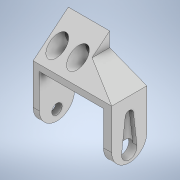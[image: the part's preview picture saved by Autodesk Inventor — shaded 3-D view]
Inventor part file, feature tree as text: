
AUTODESK INVENTOR PART (.ipt)
format: ipt  version: 2022.1 (Build 261234000, 234)  size: 200,192 bytes
history: native  units: mm
features: extrude x8, sketch x7, fillet x1
ambient origin geometry x8: Origin, YZ Plane, XZ Plane, XY Plane, X Axis, Y Axis, Z Axis, Center Point
bodies: Solid1 (feature_tree)
feature tree (16):
  extrude  "Extrusion1"  Depth=3.0mm
  extrude  "Extrusion2"  Depth=4.0mm
  extrude  "Extrusion4"  Depth=38.0mm
  extrude  "Extrusion5"  Depth=17.0mm TaperAngle=0.0deg
  extrude  "Extrusion10"  Depth=17.0mm TaperAngle=0.0deg
  extrude  "Extrusion11"  Depth=17.0mm
  extrude  "Extrusion12"  Depth=8.5mm
  fillet  "Fillet2"  Radius=8.5mm
  extrude  "Extrusion13"  Depth=2.0mm
  sketch  "Sketch1"  dims[d0=3.0mm d1=25.0mm]
  sketch  "Sketch2"  dims[d2=4.0mm d3=25.0mm]
  sketch  "Sketch5"  dims[d4=31.0mm d5=38.0mm]
  sketch  "Sketch10"  dims[d6=17.0mm d7=17.0mm d8=0.0mm]
  sketch  "Sketch11"  dims[d9=14.0mm d10=17.0mm d11=0.0mm]
  sketch  "Sketch12"  dims[d17=17.0mm d18=7.0mm]
  sketch  "Sketch13"  dims[d19=7.0mm d20=8.5mm d22=8.5mm d23=5.0mm d24=14.0mm d25=0.0mm d26=3.0mm d27=3.0mm d28=14.0mm d29=0.0mm d48=5.0mm d49=20.0mm d50=18.0mm d51=7.0mm d52=10.0mm d53=0.0mm d54=7.5mm d55=5.0mm d56=8.5mm d57=10.0mm d58=0.0mm d59=5.0mm d60=5.0mm d61=8.5mm d62=10.0mm d63=0.0mm d64=8.5mm d65=4.0mm d66=15.0mm d67=0.0mm d68=2.0mm d69=0.0mm]
